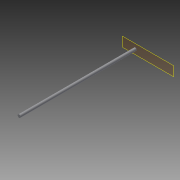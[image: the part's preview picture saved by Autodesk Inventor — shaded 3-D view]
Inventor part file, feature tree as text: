
AUTODESK INVENTOR PART (.ipt)
format: ipt  version: 2015 (Build 190159000, 159)  size: 69,120 bytes
history: native  units: in
note: dims shown in document units (in); Inventor stores cm internally (conversion verified against a paired STEP export)
features: reference x2, plane x1, extrude x1, sketch x1
ambient origin geometry x8: Origin, YZ Plane, XZ Plane, XY Plane, X Axis, Y Axis, Z Axis, Center Point
bodies: Solid1 (feature_tree)
feature tree (5):
  plane  "Work Plane1"
  extrude  "Extrusion1"  [1 undecoded]
  sketch  "Sketch1"  dims[d2=10.0in d3=0.0in]
  reference  "Reference1"
  reference  "Reference2"
note: 1 required parameter value undecoded (feature->parameter linkage not recoverable at this tier; creation-order binding heuristic only, values carry confidence <= 0.55)
